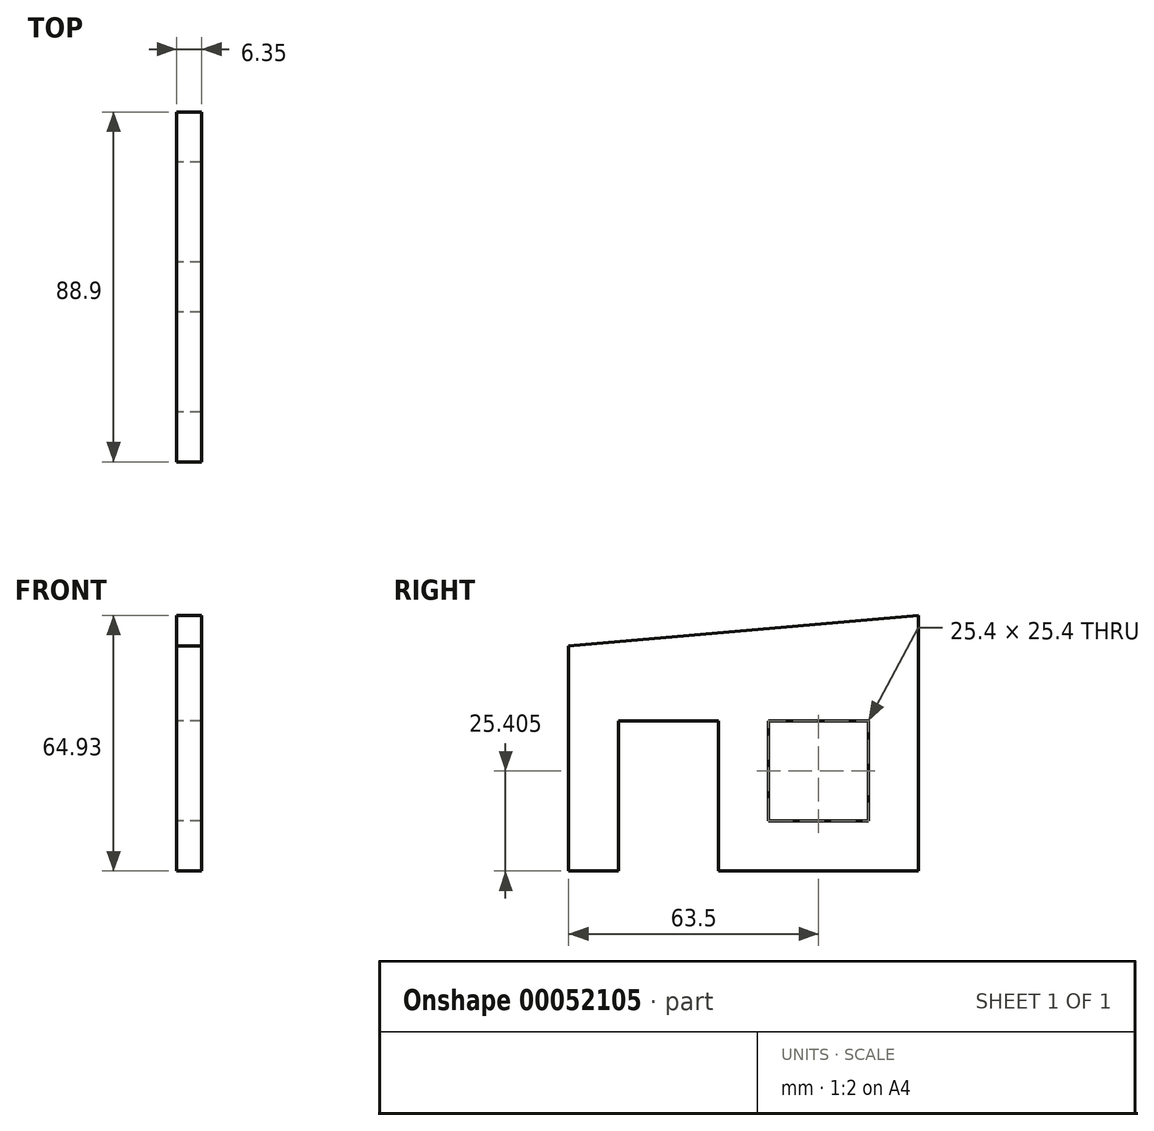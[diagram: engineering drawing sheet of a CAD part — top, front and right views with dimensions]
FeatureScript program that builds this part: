
annotation { "Feature Type Name" : "Feature", "Feature Type Description" : "" }
export const myFeature = defineFeature(function(context is Context, id is Id, definition is map)
    precondition{}
    {
        {
            var Q0;
            Q0=qCreatedBy(makeId("Right.planeOp"),FACE);
            var sketch = newSketch(context, id + "F0", { "sketchPlane" : qUnion([Q0])});
            skLineSegment(sketch, "E0.rect.bottom", {"start": v(-44.45, 28.58) * mm, "end": v(44.45, 28.58) * mm, "construction": true});
            skLineSegment(sketch, "E0.rect.top", {"start": v(-44.45, -28.57) * mm, "end": v(44.45, -28.57) * mm});
            skLineSegment(sketch, "E0.rect.left", {"start": v(-44.45, 28.58) * mm, "end": v(-44.45, -28.57) * mm});
            skLineSegment(sketch, "E0.rect.right", {"start": v(44.45, 28.58) * mm, "end": v(44.45, -28.57) * mm});
            skPoint(sketch, "E0.rect.middle", {"position": v(0, 0) * mm});
            skLineSegment(sketch, "E1", {"start": v(-44.45, 28.58) * mm, "end": v(44.45, 36.35) * mm});
            skLineSegment(sketch, "E2", {"start": v(44.45, 36.35) * mm, "end": v(44.45, 28.58) * mm});
            skSolve(sketch);
        }
        {
            var Q0;
            Q0 = qSketchRegion(id + "F0", true);
            extrude(context, id + "F1", {"entities" : qUnion([Q0]), "depth" : 6.35 * mm});
        }
        {
            var Q0;
            Q0=qCreatedBy(makeId("Right.planeOp"),FACE);
            var sketch = newSketch(context, id + "F2", { "sketchPlane" : qUnion([Q0])});
            skLineSegment(sketch, "E3.bottom", {"start": v(-31.75, -28.57) * mm, "end": v(-6.35, -28.57) * mm});
            skLineSegment(sketch, "E3.top", {"start": v(-31.75, 9.53) * mm, "end": v(-6.35, 9.53) * mm});
            skLineSegment(sketch, "E3.left", {"start": v(-31.75, -28.57) * mm, "end": v(-31.75, 9.53) * mm});
            skLineSegment(sketch, "E3.right", {"start": v(-6.35, -28.57) * mm, "end": v(-6.35, 9.53) * mm});
            skLineSegment(sketch, "E4.bottom", {"start": v(31.75, -15.87) * mm, "end": v(6.35, -15.87) * mm});
            skLineSegment(sketch, "E4.top", {"start": v(31.75, 9.53) * mm, "end": v(6.35, 9.53) * mm});
            skLineSegment(sketch, "E4.left", {"start": v(31.75, -15.87) * mm, "end": v(31.75, 9.53) * mm});
            skLineSegment(sketch, "E4.right", {"start": v(6.35, -15.87) * mm, "end": v(6.35, 9.53) * mm});
            skSolve(sketch);
        }
        {
            var Q0;
            Q0 = qSketchRegion(id + "F2", true);
            extrude(context, id + "F3", {"entities" : qUnion([Q0]), "operationType" : NewBodyOperationType.REMOVE, "endBound" : BoundingType.THROUGH_ALL, "depth" : 25.4 * mm});
        }
    });
